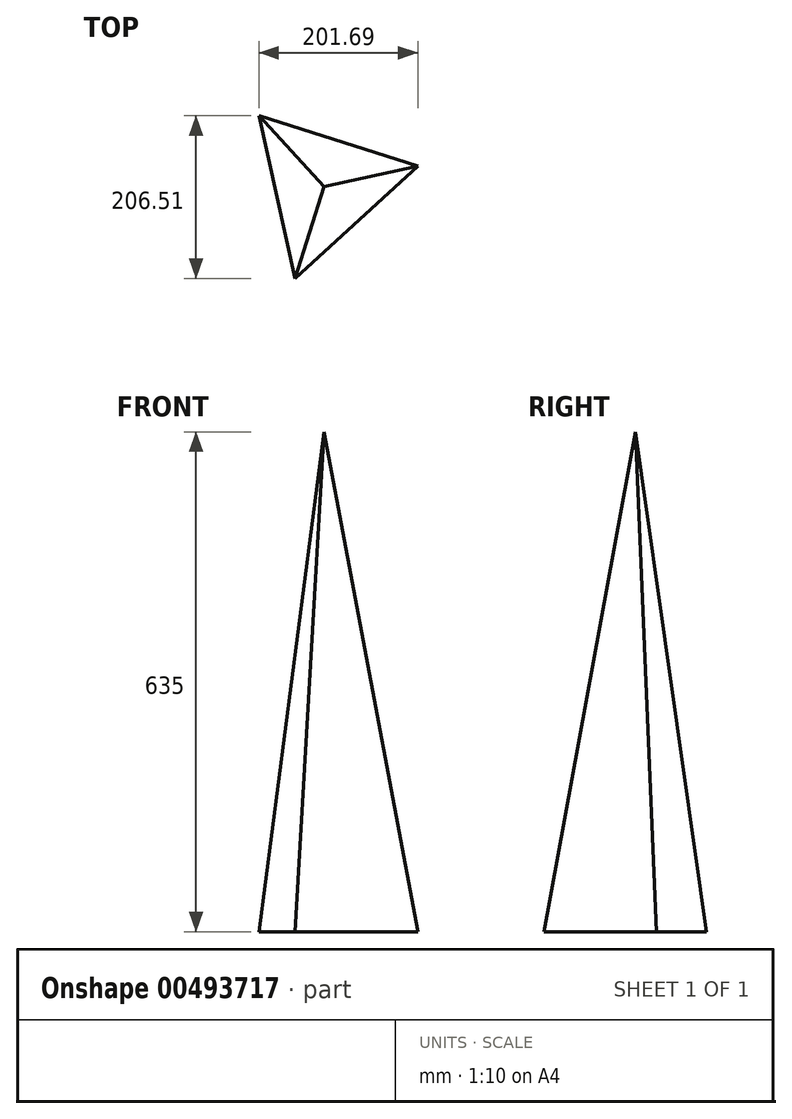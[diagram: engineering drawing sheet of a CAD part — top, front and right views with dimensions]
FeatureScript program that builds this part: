
annotation { "Feature Type Name" : "Feature", "Feature Type Description" : "" }
export const myFeature = defineFeature(function(context is Context, id is Id, definition is map)
    precondition{}
    {
        {
            var Q0;
            Q0=qCreatedBy(makeId("Top.planeOp"),FACE);
            var sketch = newSketch(context, id + "F0", { "sketchPlane" : qUnion([Q0])});
            skCircle(sketch, "E0.cCircle", {"center": v(0, 0) * mm, "radius": 122.11 * mm, "construction": true});
            skLineSegment(sketch, "E0.0", {"start": v(-82.46, 90.07) * mm, "end": v(119.23, 26.38) * mm});
            skLineSegment(sketch, "E0.1", {"start": v(119.23, 26.38) * mm, "end": v(-36.77, -116.44) * mm});
            skLineSegment(sketch, "E0.2", {"start": v(-36.77, -116.44) * mm, "end": v(-82.46, 90.07) * mm});
            skSolve(sketch);
        }
        {
            var Q0;
            Q0=qCreatedBy(makeId("Top.planeOp"),FACE);
            cPlane(context, id + "F1", {"entities" : qUnion([Q0]), "cplaneType" : CPlaneType.OFFSET, "offset" : 635 * mm, "width" : 152.4 * mm, "height" : 152.4 * mm});
        }
        {
            var Q0;
            Q0=qCreatedBy(id+"F1.planeOp",FACE);
            var sketch = newSketch(context, id + "F2", { "sketchPlane" : qUnion([Q0])});
            skPoint(sketch, "E1", {"position": v(0, 0) * mm});
            skSolve(sketch);
        }
        {
            var Q0;
            Q0=makeQuery(id+"F0.imprint","IMPRINT",FACE,{"disambiguationData":[TD([[makeQuery(id+"F0.imprint","IMPRINT",EDGE,{"derivedFrom":sQuery(id+"F0.wireOp",EDGE,"E0.0")}),-1.0]])]});
            var Q1;
            Q1=sQuery(id+"F2.wireOp",VERTEX,"E1");
            loft(context, id + "F3", {"sheetProfilesArray" : [{ "sheetProfileEntities" : qUnion([Q0]) }, { "sheetProfileEntities" : qUnion([Q1]) }]});
        }
    });
